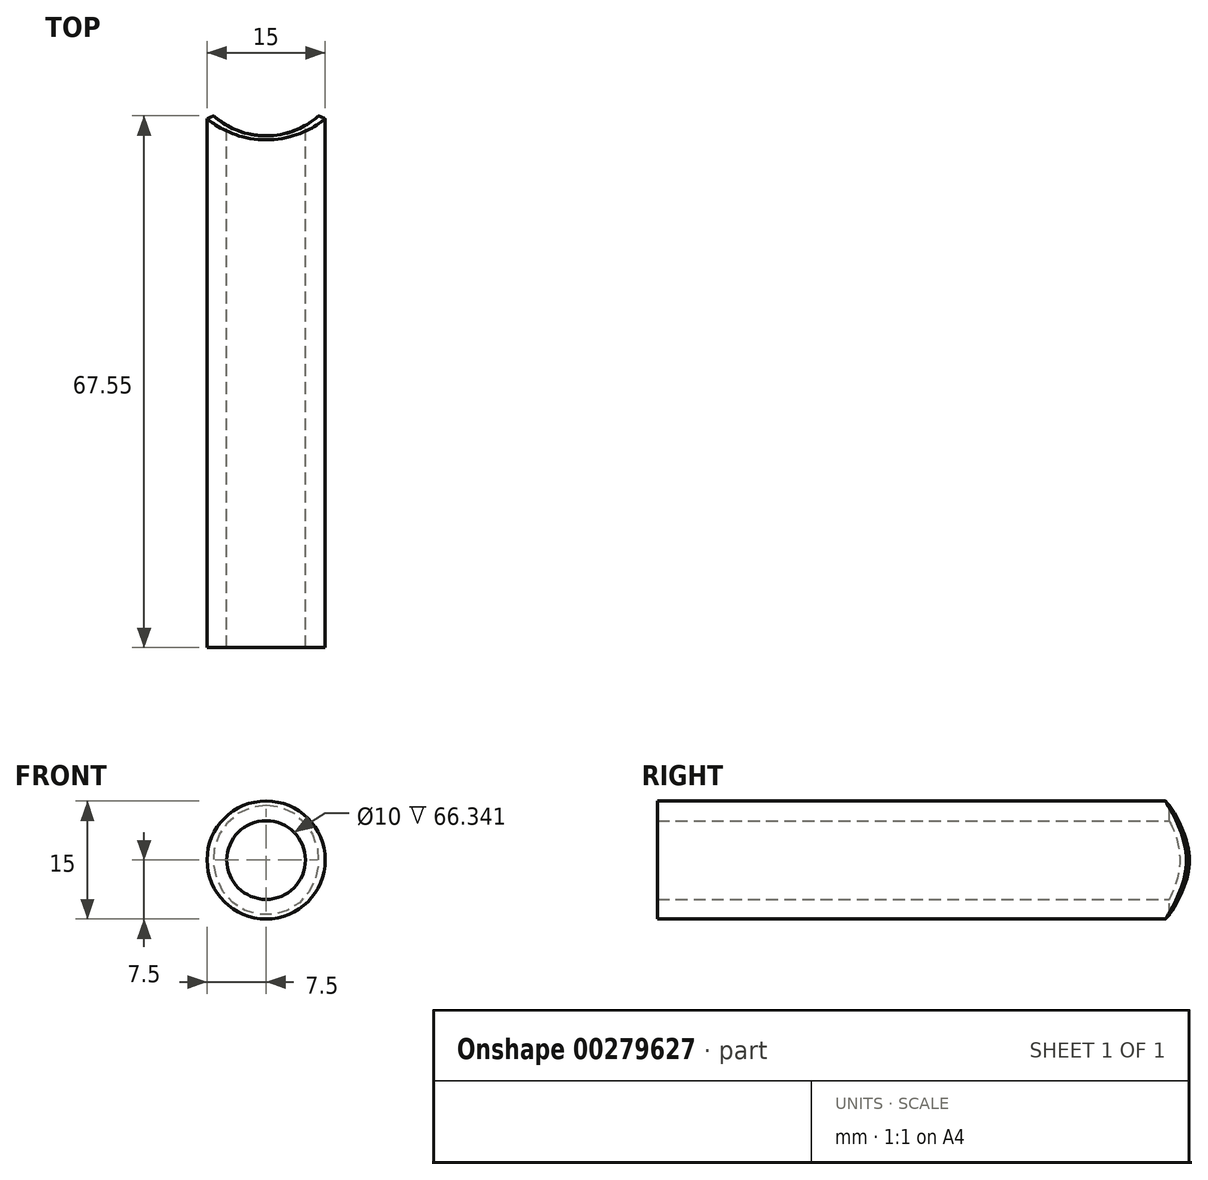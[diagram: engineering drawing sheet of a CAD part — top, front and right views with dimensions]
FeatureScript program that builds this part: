
annotation { "Feature Type Name" : "Feature", "Feature Type Description" : "" }
export const myFeature = defineFeature(function(context is Context, id is Id, definition is map)
    precondition{}
    {
        {
            var Q0;
            Q0=qCreatedBy(makeId("Front.planeOp"),FACE);
            var sketch = newSketch(context, id + "F0", { "sketchPlane" : qUnion([Q0])});
            skCircle(sketch, "E0", {"center": v(0, 0) * mm, "radius": 7.5 * mm});
            skCircle(sketch, "E1", {"center": v(0, 0) * mm, "radius": 5 * mm});
            skSolve(sketch);
        }
        {
            var Q0;
            Q0 = qSketchRegion(id + "F0", true);
            extrude(context, id + "F1", {"entities" : qUnion([Q0]), "depth" : 75 * mm});
        }
        {
            var Q0;
            Q0=qCreatedBy(makeId("Right.planeOp"),FACE);
            var sketch = newSketch(context, id + "F2", { "sketchPlane" : qUnion([Q0])});
            skLineSegment(sketch, "E2", {"start": v(10, -26.26) * mm, "end": v(10, 33.54) * mm});
            skLineSegment(sketch, "E3", {"start": v(0, -31.46) * mm, "end": v(0, 43.94) * mm, "construction": true});
            skLineSegment(sketch, "E4", {"start": v(10, -26.26) * mm, "end": v(0, -26.26) * mm});
            skLineSegment(sketch, "E5", {"start": v(0, -26.26) * mm, "end": v(0, 33.54) * mm});
            skLineSegment(sketch, "E6", {"start": v(0, 33.54) * mm, "end": v(10, 33.54) * mm});
            skSolve(sketch);
        }
        {
            var Q0;
            Q0 = qSketchRegion(id + "F2", true);
            var Q1;
            Q1=sQuery(id+"F2.wireOp",EDGE,"E3");
            revolve(context, id + "F3", {"operationType" : NewBodyOperationType.REMOVE, "entities" : qUnion([Q0]), "axis" : qUnion([Q1]), "revolveType" : RevolveType.FULL, "oppositeDirection" : true});
        }
        {
            var Q0;
            Q0=makeQuery(id+"F3.boolean.opBoolean","INTERSECT",EDGE,{"derivedFrom":[makeQuery(id+"F1.opExtrude","SWEPT_FACE",FACE,{"disambiguationData":[OSD([sQuery(id+"F0.wireOp",EDGE,"E0")])]}),makeQuery(id+"F3.opRevolve","SWEPT_FACE",FACE,{"disambiguationData":[OSD([sQuery(id+"F2.wireOp",EDGE,"E2")])]})]});
            chamfer(context, id + "F4", {"entities" : qUnion([Q0]), "width" : 0.5 * mm, "tangentPropagation" : true});
        }
    });
